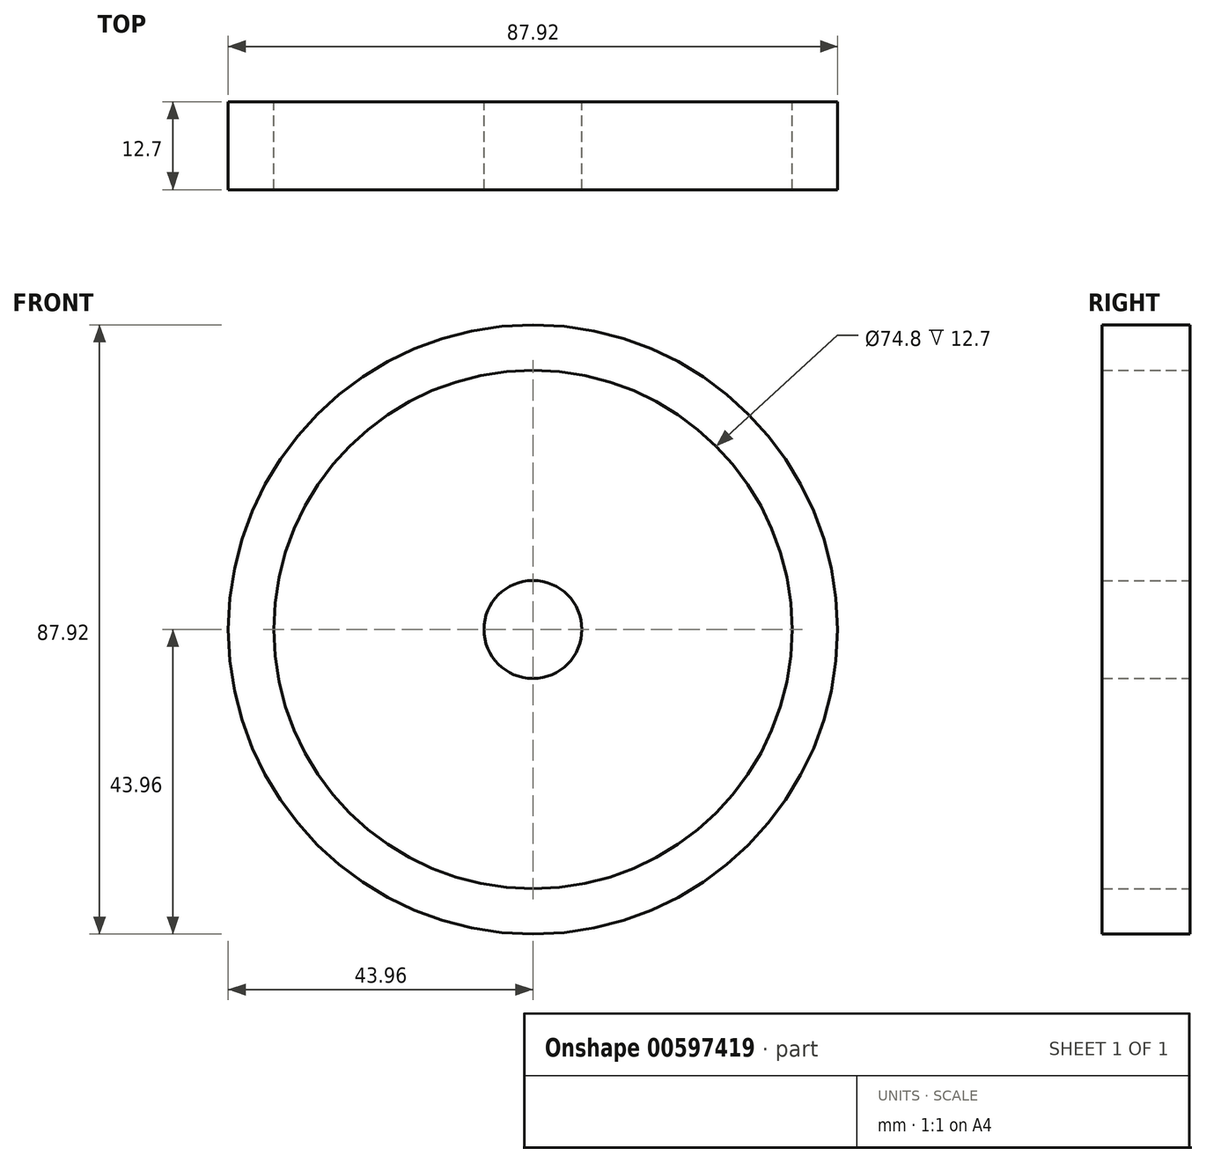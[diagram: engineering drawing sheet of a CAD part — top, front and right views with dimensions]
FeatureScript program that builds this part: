
annotation { "Feature Type Name" : "Feature", "Feature Type Description" : "" }
export const myFeature = defineFeature(function(context is Context, id is Id, definition is map)
    precondition{}
    {
        {
            var Q0;
            Q0=qCreatedBy(makeId("Front.planeOp"),FACE);
            var sketch = newSketch(context, id + "F0", { "sketchPlane" : qUnion([Q0])});
            skCircle(sketch, "E0", {"center": v(0, 0) * mm, "radius": 43.96 * mm});
            skCircle(sketch, "E1", {"center": v(0, 0) * mm, "radius": 37.4 * mm});
            skSolve(sketch);
        }
        {
            var Q0;
            Q0 = qSketchRegion(id + "F0", true);
            extrude(context, id + "F1", {"entities" : qUnion([Q0]), "depth" : 12.7 * mm, "offsetDistance" : 25.4 * mm});
        }
        {
            var Q0;
            Q0=qCreatedBy(makeId("Front.planeOp"),FACE);
            var sketch = newSketch(context, id + "F2", { "sketchPlane" : qUnion([Q0])});
            skCircle(sketch, "E2", {"center": v(0, 0) * mm, "radius": 7.06 * mm});
            skSolve(sketch);
        }
        {
            var Q0;
            Q0 = qSketchRegion(id + "F2", true);
            extrude(context, id + "F3", {"entities" : qUnion([Q0]), "depth" : 12.7 * mm, "offsetDistance" : 25.4 * mm});
        }
    });
